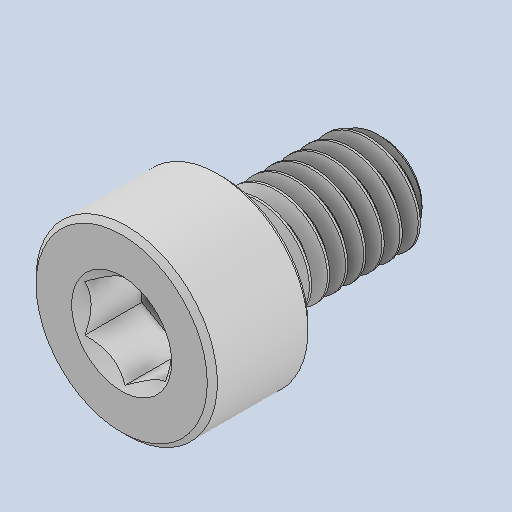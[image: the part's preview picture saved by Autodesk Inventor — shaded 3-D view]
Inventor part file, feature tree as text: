
AUTODESK INVENTOR PART (.ipt)
format: ipt  version: 2025 (Build 290162000, 162)  size: 416,768 bytes
history: native  units: in
note: dims shown in document units (in); Inventor stores cm internally (conversion verified against a paired STEP export)
features: revolve x1
ambient origin geometry x8: Origin, YZ Plane, XZ Plane, XY Plane, X Axis, Y Axis, Z Axis, Center Point
bodies: Solid1 (feature_tree)
feature tree (1):
  revolve  "Revolve2"  [1 undecoded]
note: 1 required parameter value undecoded (feature->parameter linkage not recoverable at this tier; creation-order binding heuristic only, values carry confidence <= 0.55)
